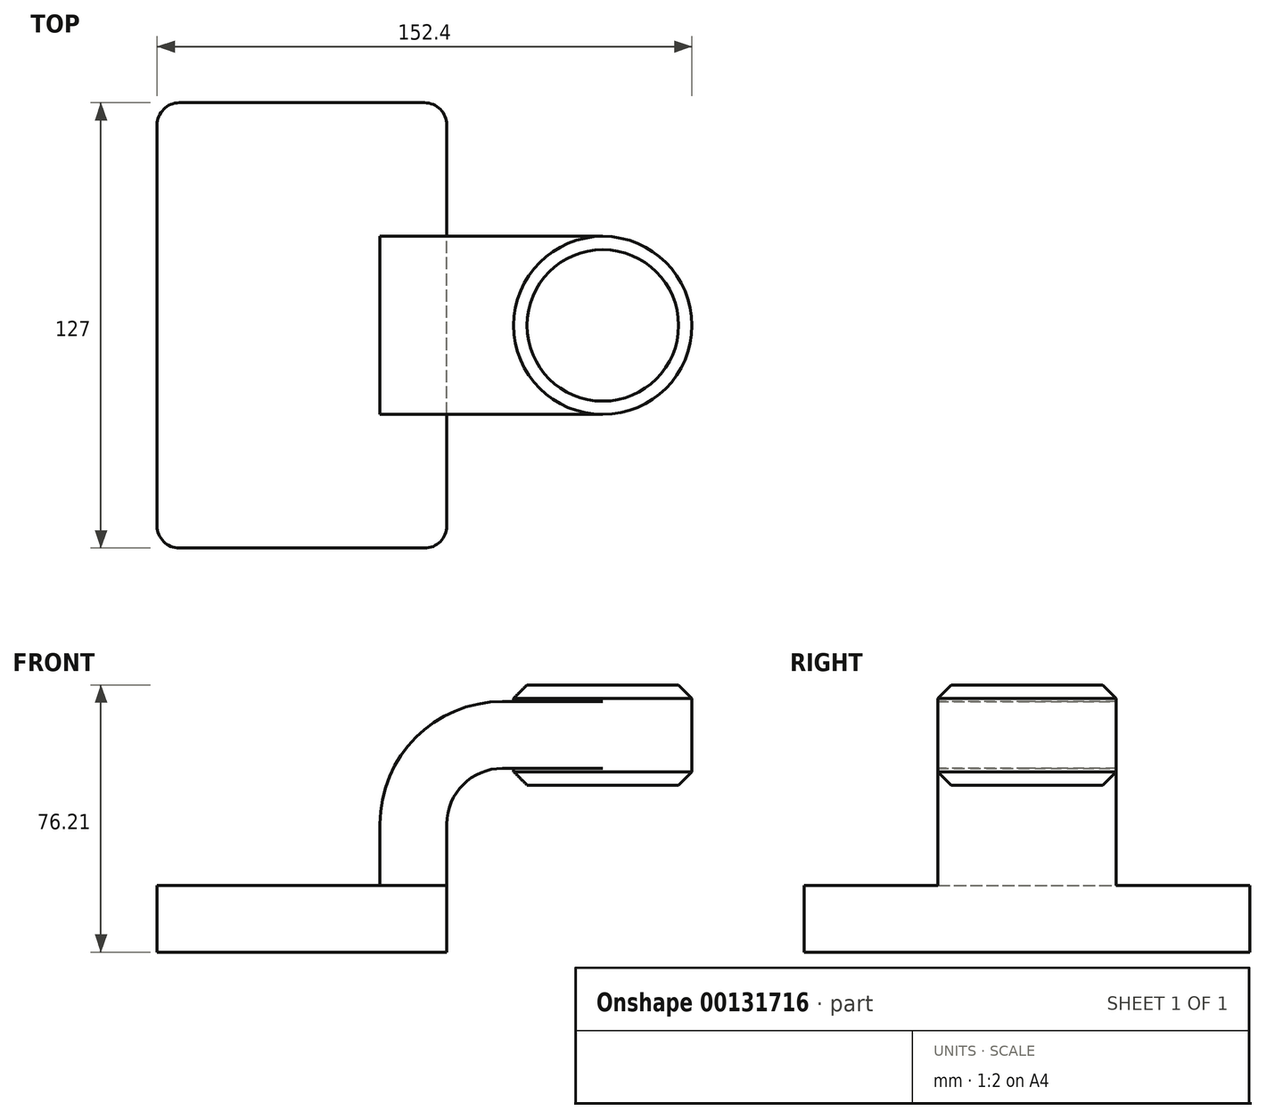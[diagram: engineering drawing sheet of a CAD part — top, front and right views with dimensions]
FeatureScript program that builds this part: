
annotation { "Feature Type Name" : "Feature", "Feature Type Description" : "" }
export const myFeature = defineFeature(function(context is Context, id is Id, definition is map)
    precondition{}
    {
        {
            var Q0;
            Q0=qCreatedBy(makeId("Front.planeOp"),FACE);
            var sketch = newSketch(context, id + "F0", { "sketchPlane" : qUnion([Q0])});
            skLineSegment(sketch, "E0.bottom", {"start": v(41.28, -9.52) * mm, "end": v(-41.28, -9.53) * mm});
            skLineSegment(sketch, "E0.top", {"start": v(41.28, 9.53) * mm, "end": v(-41.28, 9.52) * mm});
            skLineSegment(sketch, "E0.left", {"start": v(41.28, -9.52) * mm, "end": v(41.28, 9.53) * mm});
            skLineSegment(sketch, "E0.right", {"start": v(-41.28, -9.53) * mm, "end": v(-41.28, 9.52) * mm});
            skPoint(sketch, "E0.middle", {"position": v(0, 0) * mm});
            skLineSegment(sketch, "E1.bottom", {"start": v(111.12, 38.1) * mm, "end": v(60.32, 38.1) * mm});
            skLineSegment(sketch, "E1.top", {"start": v(111.12, 66.68) * mm, "end": v(60.32, 66.68) * mm});
            skLineSegment(sketch, "E1.left", {"start": v(111.12, 38.1) * mm, "end": v(111.12, 66.68) * mm});
            skLineSegment(sketch, "E1.right", {"start": v(60.32, 38.1) * mm, "end": v(60.32, 66.68) * mm});
            skPoint(sketch, "E1.middle", {"position": v(85.72, 52.39) * mm});
            skLineSegment(sketch, "E2", {"start": v(41.28, 9.53) * mm, "end": v(41.28, 27) * mm});
            skArc(sketch, "E3", {"start": v(41.28, 27) * mm, "mid": v(45.92, 38.23) * mm, "end": v(57.15, 42.88) * mm});
            skLineSegment(sketch, "E4", {"start": v(57.15, 42.88) * mm, "end": v(85.72, 42.88) * mm});
            skLineSegment(sketch, "E5.0", {"start": v(57.15, 61.93) * mm, "end": v(85.72, 61.93) * mm});
            skArc(sketch, "E5.1", {"start": v(22.23, 27) * mm, "mid": v(32.45, 51.7) * mm, "end": v(57.15, 61.93) * mm});
            skLineSegment(sketch, "E5.2", {"start": v(22.23, 9.53) * mm, "end": v(22.23, 27) * mm});
            skLineSegment(sketch, "E6", {"start": v(85.72, 66.68) * mm, "end": v(85.72, 38.1) * mm});
            skFitSpline(sketch, "E7", {"points": [v(-41.28, 9.52) * mm, v(57.15, 61.93) * mm], "startDerivative": vector(2.69, 112.7) * mm, "endDerivative": vector(143.6, -0.03) * mm});
            skSolve(sketch);
        }
        {
            var Q0;
            Q0=makeQuery(id+"F0.imprint","IMPRINT",FACE,{"disambiguationData":[TD([[makeQuery(id+"F0.imprint","IMPRINT",EDGE,{"derivedFrom":sQuery(id+"F0.wireOp",EDGE,"E0.bottom")}),-1.0]])]});
            extrude(context, id + "F1", {"entities" : qUnion([Q0]), "endBound" : BoundingType.SYMMETRIC, "depth" : 127 * mm});
        }
        {
            var Q0;
            {var subQ1=sQuery(id+"F0.wireOp",EDGE,"E2");Q0=makeQuery(id+"F0.imprint","IMPRINT",FACE,{"disambiguationData":[TD([[makeQuery(id+"F0.imprint","IMPRINT",EDGE,{"derivedFrom":subQ1}),1.0]])]});}
            var Q1;
            {var subQ0=sQuery(id+"F0.wireOp",EDGE,"E4");var subQ1=sQuery(id+"F0.wireOp",EDGE,"E1.right");var subQ2=makeQuery(id+"F0.imprint","INTERSECT",VERTEX,{"derivedFrom":[subQ1,subQ0]});Q1=makeQuery(id+"F0.imprint","IMPRINT",FACE,{"disambiguationData":[TD([[makeQuery(id+"F0.imprint","IMPRINT",EDGE,{"disambiguationData":[TD([[subQ2,-1.0]])],"derivedFrom":subQ1}),-1.0]])]});}
            extrude(context, id + "F2", {"entities" : qUnion([Q0, Q1]), "operationType" : NewBodyOperationType.ADD, "endBound" : BoundingType.SYMMETRIC, "depth" : 50.8 * mm});
        }
        {
            var Q0;
            Q0=makeQuery(id+"F0.imprint","IMPRINT",FACE,{"disambiguationData":[TD([[makeQuery(id+"F0.imprint","IMPRINT",EDGE,{"derivedFrom":sQuery(id+"F0.wireOp",EDGE,"E5.1")}),1.0]])]});
            extrude(context, id + "F3", {"entities" : qUnion([Q0]), "operationType" : NewBodyOperationType.ADD, "endBound" : BoundingType.SYMMETRIC, "depth" : 15.88 * mm});
        }
        {
            var Q0;
            {var subQ0=sQuery(id+"F0.wireOp",EDGE,"E1.left");Q0=makeQuery(id+"F0.imprint","IMPRINT",FACE,{"disambiguationData":[TD([[makeQuery(id+"F0.imprint","IMPRINT",EDGE,{"derivedFrom":subQ0}),1.0]])]});}
            var Q1;
            Q1=sQuery(id+"F0.wireOp",EDGE,"E6");
            revolve(context, id + "F4", {"operationType" : NewBodyOperationType.ADD, "entities" : qUnion([Q0]), "axis" : qUnion([Q1]), "revolveType" : RevolveType.FULL});
        }
        {
            var Q0;
            Q0=makeQuery(id+"F1.opExtrude","CAP_EDGE",EDGE,{"disambiguationData":[OSD([sQuery(id+"F0.wireOp",EDGE,"E0.left")])],"isStart":true});
            var Q1;
            Q1=makeQuery(id+"F1.opExtrude","CAP_EDGE",EDGE,{"disambiguationData":[OSD([sQuery(id+"F0.wireOp",EDGE,"E0.right")])],"isStart":true});
            var Q2;
            Q2=makeQuery(id+"F1.opExtrude","CAP_EDGE",EDGE,{"disambiguationData":[OSD([sQuery(id+"F0.wireOp",EDGE,"E0.left")])],"isStart":false});
            var Q3;
            Q3=makeQuery(id+"F1.opExtrude","CAP_EDGE",EDGE,{"disambiguationData":[OSD([sQuery(id+"F0.wireOp",EDGE,"E0.right")])],"isStart":false});
            fillet(context, id + "F5", {"entities" : qUnion([Q0, Q1, Q2, Q3]), "radius" : 6.35 * mm, "tangentPropagation" : true, "allowEdgeOverflow" : false});
        }
        {
            var Q0;
            Q0=makeQuery(id+"F4.opRevolve","SWEPT_EDGE",EDGE,{"disambiguationData":[OSD([sQuery(id+"F0.wireOp",EDGE,"E1.top"),sQuery(id+"F0.wireOp",EDGE,"E1.left")])]});
            var Q1;
            Q1=makeQuery(id+"F4.opRevolve","SWEPT_EDGE",EDGE,{"disambiguationData":[OSD([sQuery(id+"F0.wireOp",EDGE,"E1.bottom"),sQuery(id+"F0.wireOp",EDGE,"E1.left")])]});
            chamfer(context, id + "F6", {"entities" : qUnion([Q0, Q1]), "width" : 3.8 * mm, "tangentPropagation" : true});
        }
    });
